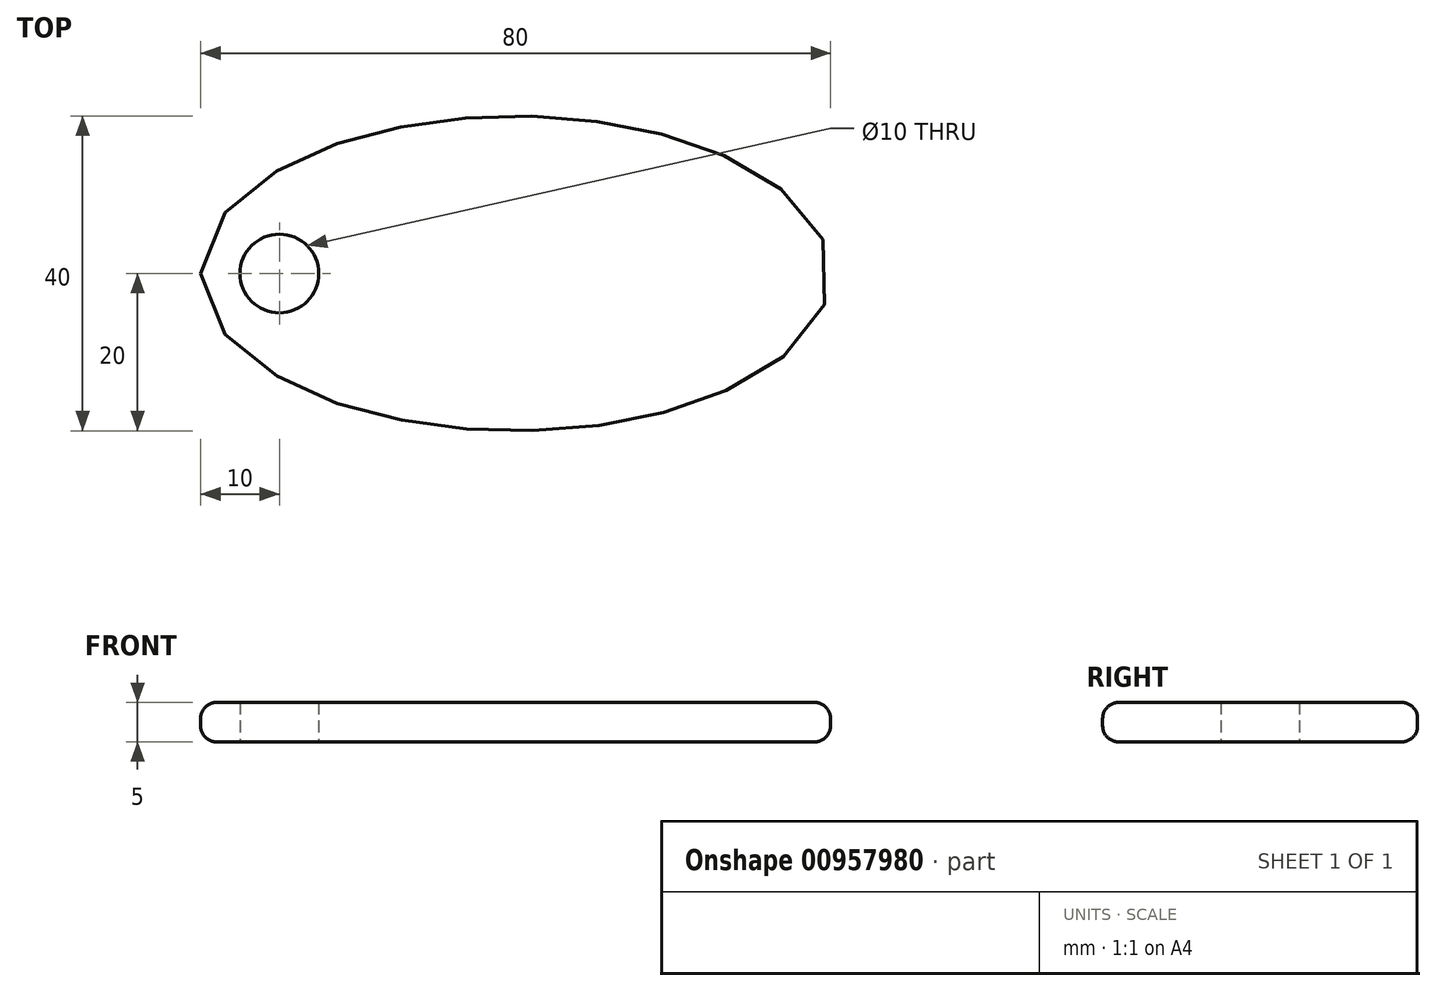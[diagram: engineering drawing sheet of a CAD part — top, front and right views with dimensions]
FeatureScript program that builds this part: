
annotation { "Feature Type Name" : "Feature", "Feature Type Description" : "" }
export const myFeature = defineFeature(function(context is Context, id is Id, definition is map)
    precondition{}
    {
        {
            var Q0;
            Q0=qCreatedBy(makeId("Top.planeOp"),FACE);
            var sketch = newSketch(context, id + "F0", { "sketchPlane" : qUnion([Q0])});
            skEllipse(sketch, "E0", {"center": v(0, 0) * mm, "majorRadius": 40 * mm, "minorRadius": 20 * mm, "majorAxis": v(-1, 0)});
            skCircle(sketch, "E1", {"center": v(-30, 0) * mm, "radius": 5 * mm});
            skSolve(sketch);
        }
        {
            var Q0;
            Q0=makeQuery(id+"F0.imprint","IMPRINT",FACE,{"disambiguationData":[TD([[makeQuery(id+"F0.imprint","IMPRINT",EDGE,{"derivedFrom":sQuery(id+"F0.wireOp",EDGE,"E0")}),1.0]])]});
            extrude(context, id + "F1", {"entities" : qUnion([Q0]), "depth" : 5 * mm, "offsetDistance" : 25 * mm});
        }
        {
            var Q0;
            Q0=makeQuery(id+"F1.opExtrude","CAP_EDGE",EDGE,{"disambiguationData":[OSD([sQuery(id+"F0.wireOp",EDGE,"E0")])],"isStart":false});
            var Q1;
            Q1=makeQuery(id+"F1.opExtrude","CAP_EDGE",EDGE,{"disambiguationData":[OSD([sQuery(id+"F0.wireOp",EDGE,"E0")])],"isStart":true});
            fillet(context, id + "F2", {"entities" : qUnion([Q0, Q1]), "radius" : 2 * mm, "tangentPropagation" : true, "allowEdgeOverflow" : false});
        }
    });
